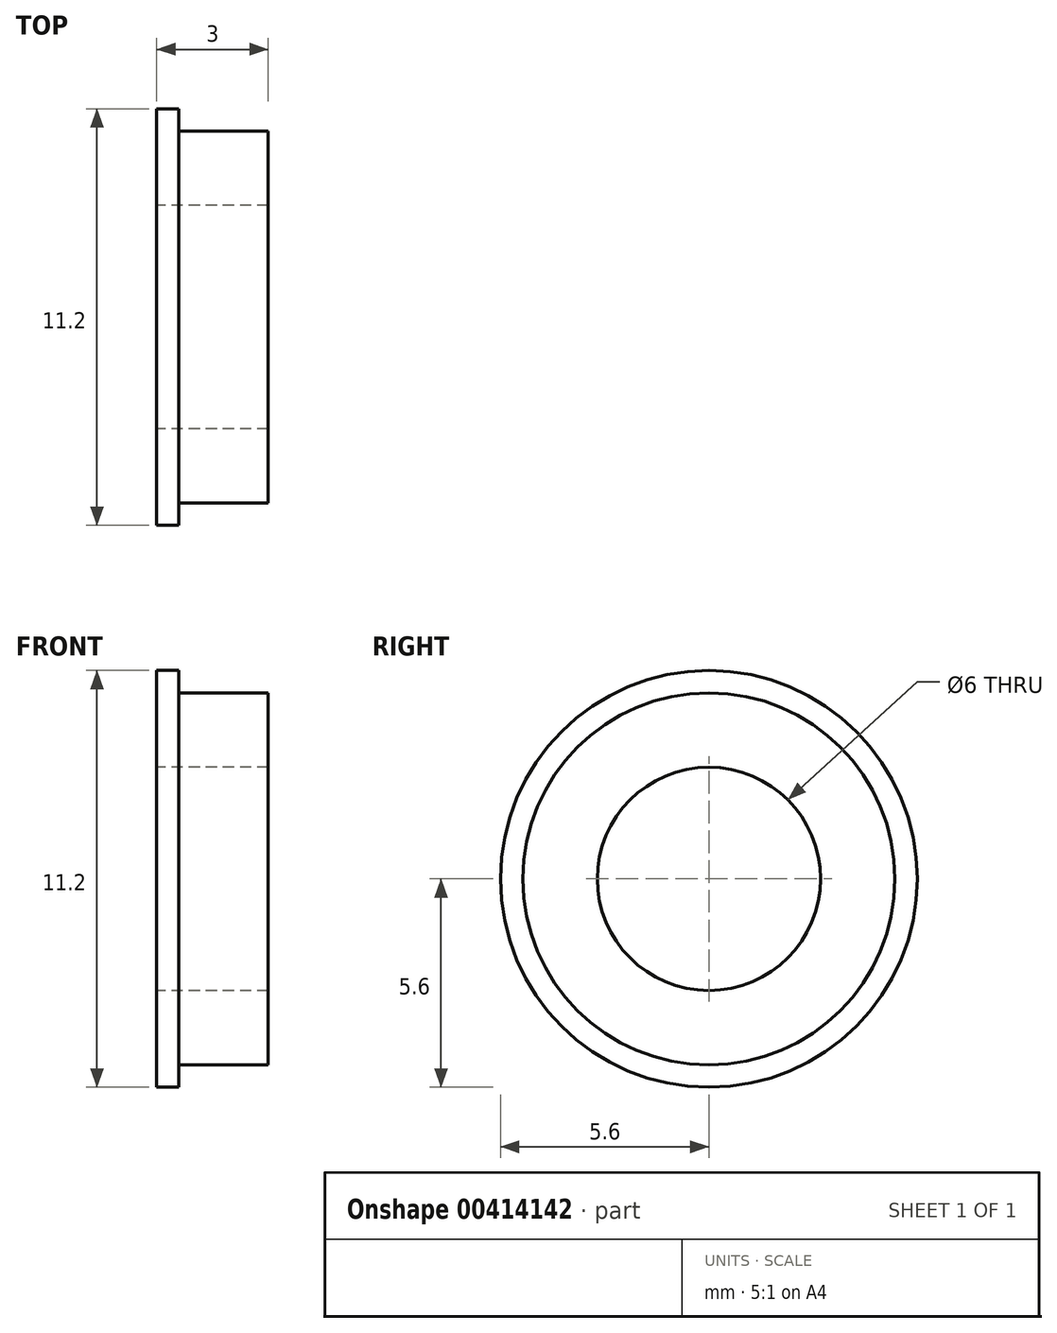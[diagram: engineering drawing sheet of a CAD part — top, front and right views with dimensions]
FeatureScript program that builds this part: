
annotation { "Feature Type Name" : "Feature", "Feature Type Description" : "" }
export const myFeature = defineFeature(function(context is Context, id is Id, definition is map)
    precondition{}
    {
        {
            var Q0;
            Q0=qCreatedBy(makeId("Front.planeOp"),FACE);
            var sketch = newSketch(context, id + "F0", { "sketchPlane" : qUnion([Q0])});
            skLineSegment(sketch, "E0", {"start": v(-5.1, 0) * mm, "end": v(5.61, 0) * mm, "construction": true});
            skLineSegment(sketch, "E1", {"start": v(0, 3) * mm, "end": v(3, 3) * mm});
            skLineSegment(sketch, "E2", {"start": v(3, 3) * mm, "end": v(3, 5) * mm});
            skLineSegment(sketch, "E3", {"start": v(3, 5) * mm, "end": v(0, 5) * mm});
            skLineSegment(sketch, "E4", {"start": v(0, 5) * mm, "end": v(0, 3) * mm});
            skSolve(sketch);
        }
        {
            var Q0;
            Q0 = qSketchRegion(id + "F0", true);
            var Q1;
            Q1=sQuery(id+"F0.wireOp",EDGE,"E0");
            revolve(context, id + "F1", {"entities" : qUnion([Q0]), "axis" : qUnion([Q1]), "revolveType" : RevolveType.FULL});
        }
        {
            var Q0;
            Q0=qCreatedBy(makeId("Front.planeOp"),FACE);
            var sketch = newSketch(context, id + "F2", { "sketchPlane" : qUnion([Q0])});
            skLineSegment(sketch, "E5", {"start": v(-8.82, 0) * mm, "end": v(8.52, 0) * mm, "construction": true});
            skLineSegment(sketch, "E6.bottom", {"start": v(0, 4.7) * mm, "end": v(0.6, 4.7) * mm});
            skLineSegment(sketch, "E6.top", {"start": v(0, 5.6) * mm, "end": v(0.6, 5.6) * mm});
            skLineSegment(sketch, "E6.left", {"start": v(0, 4.7) * mm, "end": v(0, 5.6) * mm});
            skLineSegment(sketch, "E6.right", {"start": v(0.6, 4.7) * mm, "end": v(0.6, 5.6) * mm});
            skSolve(sketch);
        }
        {
            var Q0;
            Q0 = qSketchRegion(id + "F2", true);
            var Q1;
            Q1=sQuery(id+"F2.wireOp",EDGE,"E5");
            revolve(context, id + "F3", {"operationType" : NewBodyOperationType.ADD, "entities" : qUnion([Q0]), "axis" : qUnion([Q1]), "revolveType" : RevolveType.FULL});
        }
    });
